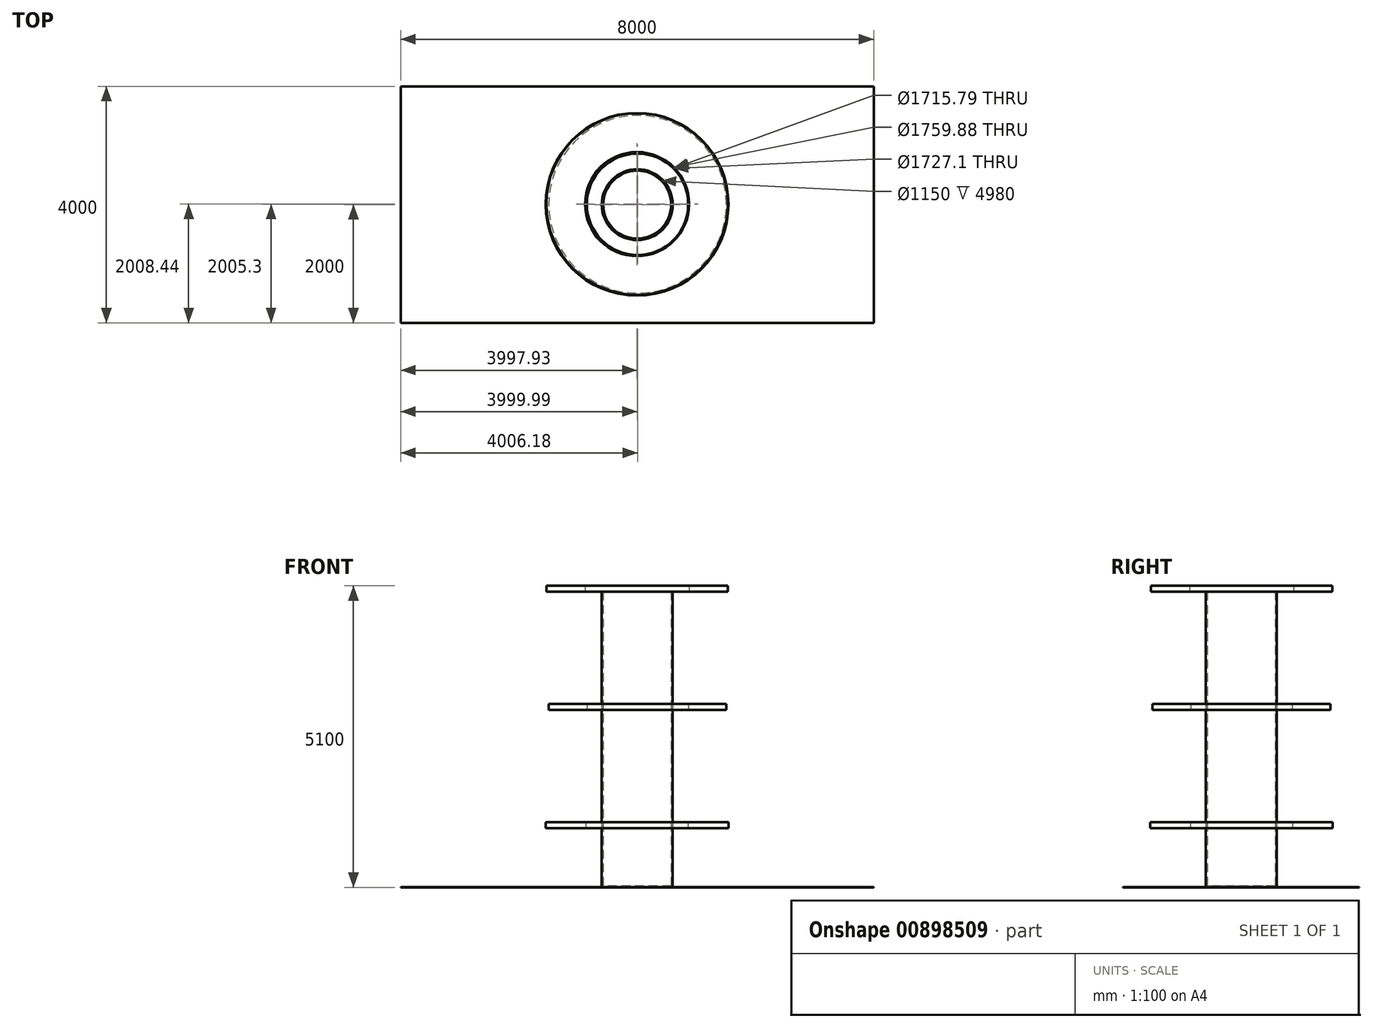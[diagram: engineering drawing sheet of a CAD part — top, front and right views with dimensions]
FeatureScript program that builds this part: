
annotation { "Feature Type Name" : "Feature", "Feature Type Description" : "" }
export const myFeature = defineFeature(function(context is Context, id is Id, definition is map)
    precondition{}
    {
        {
            var Q0;
            Q0=qCreatedBy(makeId("Top.planeOp"),FACE);
            var sketch = newSketch(context, id + "F0", { "sketchPlane" : qUnion([Q0])});
            skLineSegment(sketch, "E0.bottom", {"start": v(-127.9, 3986.47) * mm, "end": v(7872.1, 3986.47) * mm});
            skLineSegment(sketch, "E0.top", {"start": v(-127.9, -13.53) * mm, "end": v(7872.1, -13.53) * mm});
            skLineSegment(sketch, "E0.left", {"start": v(-127.9, 3986.47) * mm, "end": v(-127.9, -13.53) * mm});
            skLineSegment(sketch, "E0.right", {"start": v(7872.1, 3986.47) * mm, "end": v(7872.1, -13.53) * mm});
            skSolve(sketch);
        }
        {
            var Q0;
            Q0 = qSketchRegion(id + "F0", true);
            extrude(context, id + "F1", {"entities" : qUnion([Q0]), "depth" : 5 * mm, "offsetDistance" : 25 * mm});
        }
        {
            var Q0;
            Q0=makeQuery(id+"F1.opExtrude","CAP_FACE",FACE,{"disambiguationData":[OSD([sQuery(id+"F0.wireOp",EDGE,"E0.bottom"),sQuery(id+"F0.wireOp",EDGE,"E0.top"),sQuery(id+"F0.wireOp",EDGE,"E0.left"),sQuery(id+"F0.wireOp",EDGE,"E0.right")])],"isStart":false});
            var sketch = newSketch(context, id + "F2", { "sketchPlane" : qUnion([Q0])});
            skLineSegment(sketch, "E1", {"start": v(-127.9, 3986.47) * mm, "end": v(7872.1, -13.53) * mm, "construction": true});
            skLineSegment(sketch, "E2", {"start": v(7872.1, 3986.47) * mm, "end": v(-127.9, -13.53) * mm, "construction": true});
            skCircle(sketch, "E3", {"center": v(3872.1, 1986.47) * mm, "radius": 18.54 * mm, "construction": true});
            skCircle(sketch, "E4", {"center": v(3872.1, 1986.47) * mm, "radius": 600 * mm});
            skLineSegment(sketch, "E5", {"start": v(3872.1, 3986.47) * mm, "end": v(3872.1, 0) * mm});
            skSolve(sketch);
        }
        {
            var Q0;
            Q0 = qSketchRegion(id + "F2", true);
            extrude(context, id + "F3", {"entities" : qUnion([Q0]), "operationType" : NewBodyOperationType.ADD, "depth" : 5000 * mm, "offsetDistance" : 25 * mm});
        }
        {
            var Q0;
            Q0=makeQuery(id+"F3.opExtrude","CAP_FACE",FACE,{"disambiguationData":[OSD([sQuery(id+"F2.wireOp",EDGE,"E4")])],"isStart":false});
            shell(context, id + "F4", {"entities" : qUnion([Q0]), "thickness" : 25 * mm});
        }
        {
            var Q0;
            Q0=qCreatedBy(makeId("Top.planeOp"),FACE);
            cPlane(context, id + "F5", {"entities" : qUnion([Q0]), "cplaneType" : CPlaneType.OFFSET, "offset" : 5000 * mm, "width" : 150 * mm, "height" : 150 * mm});
        }
        {
            var Q0;
            Q0=qCreatedBy(makeId("Top.planeOp"),FACE);
            cPlane(context, id + "F6", {"entities" : qUnion([Q0]), "cplaneType" : CPlaneType.OFFSET, "offset" : 3000 * mm, "width" : 150 * mm, "height" : 150 * mm});
        }
        {
            var Q0;
            Q0=qCreatedBy(makeId("Top.planeOp"),FACE);
            cPlane(context, id + "F7", {"entities" : qUnion([Q0]), "cplaneType" : CPlaneType.OFFSET, "offset" : 1000 * mm, "width" : 150 * mm, "height" : 150 * mm});
        }
        {
            var Q0;
            Q0=qCreatedBy(id+"F5.planeOp",FACE);
            var sketch = newSketch(context, id + "F8", { "sketchPlane" : qUnion([Q0])});
            skCircle(sketch, "E6", {"center": v(3870.03, 1994.92) * mm, "radius": 1535.33 * mm});
            skCircle(sketch, "E7", {"center": v(3870.03, 1994.92) * mm, "radius": 879.94 * mm});
            skSolve(sketch);
        }
        {
            var Q0;
            Q0 = qSketchRegion(id + "F8", true);
            extrude(context, id + "F9", {"entities" : qUnion([Q0]), "depth" : 100 * mm, "offsetDistance" : 25 * mm});
        }
        {
            var Q0;
            Q0=qCreatedBy(id+"F6.planeOp",FACE);
            var sketch = newSketch(context, id + "F10", { "sketchPlane" : qUnion([Q0])});
            skCircle(sketch, "E8", {"center": v(3878.28, 1991.77) * mm, "radius": 1502.36 * mm});
            skCircle(sketch, "E9", {"center": v(3878.28, 1991.77) * mm, "radius": 857.9 * mm});
            skSolve(sketch);
        }
        {
            var Q0;
            Q0 = qSketchRegion(id + "F10", true);
            extrude(context, id + "F11", {"entities" : qUnion([Q0]), "depth" : 100 * mm, "offsetDistance" : 25 * mm});
        }
        {
            var Q0;
            Q0=qCreatedBy(id+"F7.planeOp",FACE);
            var sketch = newSketch(context, id + "F12", { "sketchPlane" : qUnion([Q0])});
            skCircle(sketch, "E10", {"center": v(3870.03, 1991.77) * mm, "radius": 1545.16 * mm});
            skCircle(sketch, "E11", {"center": v(3870.03, 1991.77) * mm, "radius": 863.55 * mm});
            skSolve(sketch);
        }
        {
            var Q0;
            Q0 = qSketchRegion(id + "F12", true);
            extrude(context, id + "F13", {"entities" : qUnion([Q0]), "depth" : 100 * mm, "offsetDistance" : 25 * mm});
        }
    });
